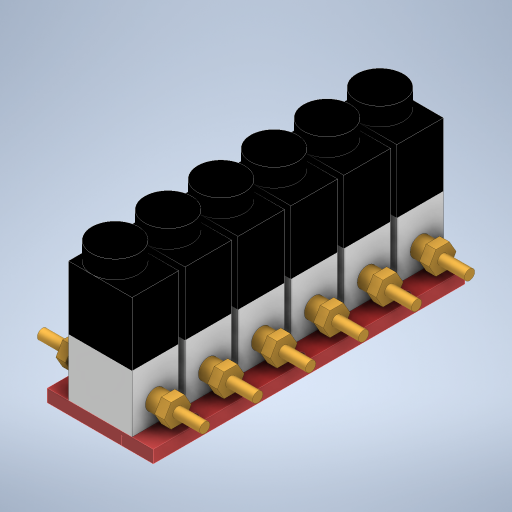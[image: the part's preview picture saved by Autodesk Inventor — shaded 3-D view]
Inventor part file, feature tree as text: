
AUTODESK INVENTOR PART (.ipt)
format: ipt  version: 2024.2 (Build 282272000, 272)  size: 733,696 bytes
history: native  units: mm
features: other x15, extrude x11, sketch x10, projected_geometry x10, mirror x2, plane x1, pattern_linear x1, chamfer x1
ambient origin geometry x8: Origin, YZ Plane, XZ Plane, XY Plane, X Axis, Y Axis, Z Axis, Center Point
bodies: Solid1 (feature_tree), Solid2 (feature_tree), Solid3 (feature_tree), Solid6 (feature_tree), Solid8 (feature_tree), Solid11 (feature_tree), Solid14 (feature_tree), Solid17 (feature_tree), Solid20 (feature_tree), Solid7 (feature_tree), Solid10 (feature_tree), Solid13 (feature_tree), Solid16 (feature_tree), Solid19 (feature_tree), Solid9 (feature_tree), Solid12 (feature_tree), Solid15 (feature_tree), Solid18 (feature_tree), Solid21 (feature_tree)
feature tree (51):
  extrude  "Extrusion1"  Depth=30.0mm
  extrude  "Extrusion2"  Depth=5.0mm
  extrude  "Extrusion3"  Depth=27.0mm TaperAngle=0.0deg
  extrude  "Extrusion4"  Depth=8.5mm TaperAngle=0.0deg
  plane  "Work Plane1"
  mirror  "Mirror1"
  extrude  "Extrusion5"  Depth=10.0mm
  extrude  "Extrusion6"  Depth=11.4mm TaperAngle=0.0deg
  sketch  "Sketch7"  dims[d17=10.6mm d18=0.0mm d19=11.0mm]
  extrude  "Extrusion7"  Depth=11.0mm
  extrude  "Extrusion8"  Depth=4.6mm
  mirror  "Mirror2"
  pattern_linear  "Rectangular Pattern1"  Count1=6 Spacing1=25.0mm
  extrude  "Extrusion9"  Depth=2.0mm
  extrude  "Extrusion10"  TaperAngle=0.0deg  [1 undecoded]
  extrude  "Extrusion11"  TaperAngle=0.0deg  [1 undecoded]
  chamfer  "Chamfer1"  Distance=10.0mm
  sketch  "Sketch1"  dims[d0=22.0mm d1=30.0mm]
  sketch  "Sketch2"  dims[d2=15.0mm d3=5.0mm]
  projected_geometry  "Projected Loop1"
  sketch  "Sketch3"  dims[d4=3.571875mm d5=27.0mm d6=0.0mm]
  sketch  "Sketch4"  dims[d7=30.0mm d8=0.0mm d9=8.5mm d10=0.0mm]
  sketch  "Sketch5"  dims[d11=10.0mm d12=9.4mm]
  sketch  "Sketch6"  dims[d13=11.4mm d14=0.0mm d15=11.4mm d16=0.0mm]
  projected_geometry  "Projected Loop2"
  projected_geometry  "Projected Loop3"
  sketch  "Sketch9"  dims[d20=4.6mm d21=0.0mm d22=4.8mm]
  projected_geometry  "Projected Loop5"
  other  "Pattern of Solid2:1"
  other  "Pattern of Solid2:2"
  other  "Pattern of Solid2:3"
  other  "Pattern of Solid2:4"
  other  "Pattern of Solid2:5"
  other  "Pattern of Solid1:6"
  other  "Pattern of Solid1:7"
  other  "Pattern of Solid1:8"
  other  "Pattern of Solid1:9"
  other  "Pattern of Solid1:10"
  other  "Pattern of Solid3:11"
  other  "Pattern of Solid3:12"
  other  "Pattern of Solid3:13"
  other  "Pattern of Solid3:14"
  other  "Pattern of Solid3:15"
  projected_geometry  "Projected Loop11"
  projected_geometry  "Projected Loop12"
  projected_geometry  "Projected Loop13"
  projected_geometry  "Projected Loop14"
  projected_geometry  "Projected Loop15"
  sketch  "Sketch10"  dims[d23=12.7mm d24=0.0mm d25=60.0mm d27=25.0mm]
  projected_geometry  "Projected Loop16"
  sketch  "Sketch11"  dims[d33=6.0mm d34=0.0mm d35=0.1mm d36=0.0mm d37=0.0mm d38=10.0mm d39=10.0mm d40=3.3mm d42=4.0mm d44=4.0mm d45=0.0mm d46=10.0mm d47=10.0mm d48=5.0mm d49=14.0mm d50=3.0mm d51=0.0mm d52=3.0mm d53=2.0mm d54=45.0deg]
note: 2 required parameter values undecoded (feature->parameter linkage not recoverable at this tier; creation-order binding heuristic only, values carry confidence <= 0.55)
